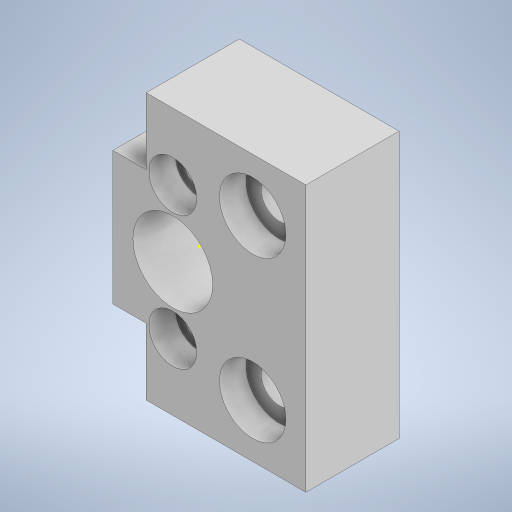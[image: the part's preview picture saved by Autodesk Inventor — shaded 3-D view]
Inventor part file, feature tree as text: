
AUTODESK INVENTOR PART (.ipt)
format: ipt  version: 2023 (Build 270158000, 158)  size: 352,768 bytes
history: native  units: mm
features: sketch x10, extrude x9, projected_geometry x4
ambient origin geometry x8: Origin, YZ Plane, XZ Plane, XY Plane, X Axis, Y Axis, Z Axis, Center Point
bodies: Solid1 (feature_tree)
feature tree (23):
  extrude  "Extrusion1"  Depth=10.0mm
  extrude  "Extrusion2"  Depth=10.0mm
  extrude  "Extrusion6"  Depth=5.0mm
  extrude  "Extrusion7"  Depth=2.4mm
  extrude  "Extrusion8"  Depth=5.0mm TaperAngle=0.0deg
  extrude  "Extrusion9"  Depth=4.0mm
  extrude  "Extrusion11"  Depth=4.0mm
  sketch  "Sketch13"  dims[d37=4.0mm d38=5.0mm]
  extrude  "Extrusion12"  Depth=5.0mm
  extrude  "Extrusion13"  Depth=5.0mm
  sketch  "Sketch1"  dims[d0=10.0mm d1=10.0mm]
  sketch  "Sketch2"  dims[d2=10.0mm d3=10.0mm]
  sketch  "Sketch7"  dims[d4=5.0mm d5=5.0mm]
  sketch  "Sketch8"  dims[d6=2.4mm d7=2.4mm]
  sketch  "Sketch9"  dims[d8=6.0mm d9=5.0mm d10=0.0mm]
  sketch  "Sketch10"  dims[d17=1.0mm d18=0.0mm d34=4.0mm]
  sketch  "Sketch12"  dims[d35=4.0mm d36=4.0mm]
  projected_geometry  "Projected Loop1"
  projected_geometry  "Projected Loop2"
  sketch  "Sketch14"  dims[d39=5.0mm d40=2.75mm]
  projected_geometry  "Projected Loop3"
  sketch  "Sketch15"  dims[d41=2.75mm d42=5.0mm d43=0.0mm d44=7.5mm d45=7.5mm d46=7.5mm d47=7.5mm d48=5.0mm d49=2.0mm d50=0.0mm d51=4.0mm d52=4.0mm d53=2.0mm d54=0.0mm d55=5.0mm d56=3.0mm d57=5.0mm d58=5.0mm d59=3.0mm d60=10.0mm d61=0.0mm d74=1.0mm d75=0.0mm d76=2.0mm d77=0.0mm d78=0.5mm d79=0.0mm d80=3.6mm d81=3.6mm]
  projected_geometry  "Projected Loop4"
